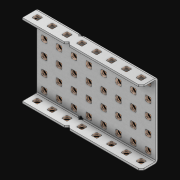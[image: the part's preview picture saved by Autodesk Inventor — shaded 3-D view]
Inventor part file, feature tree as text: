
AUTODESK INVENTOR PART (.ipt)
format: ipt  version: 2021 (Build 250183000, 183)  size: 3,014,144 bytes
history: native  units: in
note: dims shown in document units (in); Inventor stores cm internally (conversion verified against a paired STEP export)
features: extrude x57, other x56, sketch x4, thicken_offset x3, pattern_linear x3, imported_body x1
ambient origin geometry x8: Origin, YZ Plane, XZ Plane, XY Plane, X Axis, Y Axis, Z Axis, Center Point
bodies: Solid1 (feature_tree)
feature tree (124):
  thicken_offset  "Thicken1"
  thicken_offset  "Thicken2"
  thicken_offset  "Thicken3"
  pattern_linear  "Rectangular Pattern1"  Spacing1=0.001in  [1 undecoded]
  pattern_linear  "Rectangular Pattern2"  Spacing1=0.001in  [1 undecoded]
  pattern_linear  "Rectangular Pattern3"  Spacing1=0.182in  [1 undecoded]
  extrude  "Extrusion1"  Depth=0.063in TaperAngle=0.0deg
  sketch  "Sketch1"  dims[d0=0.001in]
  other  "Srf1"
  sketch  "Sketch2"  dims[d1=0.001in]
  other  "Srf2"
  sketch  "Sketch3"  dims[d2=0.001in]
  other  "Srf3"
  other  "Srf4"
  other  "Srf5"
  other  "Srf6"
  other  "Srf7"
  other  "Srf8"
  other  "Srf9"
  other  "Srf10"
  other  "Srf38"
  other  "Srf39"
  other  "Srf40"
  other  "Srf41"
  other  "Srf42"
  other  "Srf43"
  other  "Srf44"
  other  "Srf72"
  other  "Srf73"
  other  "Srf74"
  other  "Srf75"
  other  "Srf76"
  other  "Srf77"
  other  "Srf78"
  other  "Srf106"
  other  "Srf107"
  other  "Srf108"
  other  "Srf109"
  other  "Srf110"
  other  "Srf111"
  other  "Srf112"
  other  "Srf113"
  other  "Srf141"
  other  "Srf142"
  other  "Srf143"
  other  "Srf144"
  other  "Srf145"
  other  "Srf146"
  other  "Srf147"
  other  "Srf148"
  other  "Srf176"
  other  "Srf177"
  other  "Srf178"
  other  "Srf179"
  other  "Srf180"
  other  "Srf181"
  other  "Srf182"
  other  "Srf183"
  other  "Srf211"
  other  "Srf212"
  other  "Srf213"
  other  "Srf214"
  other  "Srf215"
  other  "Srf216"
  other  "Srf217"
  other  "Srf218"
  sketch  "Sketch4"  dims[d3=0.001in d4=0.001in d5=0.001in d6=0.182in d7=0.063in d8=0.0in d9=0.182in d10=0.063in d11=0.0in d12=0.182in d13=0.063in d14=0.0in d17=0.5in d18=3.1496in d20=0.5in d21=3.1496in d23=0.5in d24=1.9685in d26=0.5in d27=13.5in d28=0.0in]
  imported_body  "Imported1"
  extrude  "ExtrusionSrf1"  Depth=0.063in
  extrude  "ExtrusionSrf2"  Depth=0.063in TaperAngle=0.0deg
  extrude  "ExtrusionSrf3"  Depth=0.063in
  extrude  "ExtrusionSrf4"  Depth=0.063in TaperAngle=0.0deg
  extrude  "ExtrusionSrf5"  Depth=0.063in
  extrude  "ExtrusionSrf6"  Depth=0.063in
  extrude  "ExtrusionSrf7"  Depth=0.063in
  extrude  "ExtrusionSrf8"  Depth=0.063in
  extrude  "ExtrusionSrf9"  Depth=0.063in
  extrude  "ExtrusionSrf10"  Depth=0.063in
  extrude  "ExtrusionSrf38"  Depth=0.063in
  extrude  "ExtrusionSrf39"  TaperAngle=0.0deg  [1 undecoded]
  extrude  "ExtrusionSrf40"  [1 undecoded]
  extrude  "ExtrusionSrf41"  [1 undecoded]
  extrude  "ExtrusionSrf42"  [1 undecoded]
  extrude  "ExtrusionSrf43"  [1 undecoded]
  extrude  "ExtrusionSrf44"  [1 undecoded]
  extrude  "ExtrusionSrf72"  [1 undecoded]
  extrude  "ExtrusionSrf73"  [1 undecoded]
  extrude  "ExtrusionSrf74"  [1 undecoded]
  extrude  "ExtrusionSrf75"  [1 undecoded]
  extrude  "ExtrusionSrf76"  [1 undecoded]
  extrude  "ExtrusionSrf77"  [1 undecoded]
  extrude  "ExtrusionSrf78"  [1 undecoded]
  extrude  "ExtrusionSrf106"  [1 undecoded]
  extrude  "ExtrusionSrf107"  [1 undecoded]
  extrude  "ExtrusionSrf108"  [1 undecoded]
  extrude  "ExtrusionSrf109"  [1 undecoded]
  extrude  "ExtrusionSrf110"  [1 undecoded]
  extrude  "ExtrusionSrf111"  [1 undecoded]
  extrude  "ExtrusionSrf112"  [1 undecoded]
  extrude  "ExtrusionSrf113"  [1 undecoded]
  extrude  "ExtrusionSrf141"  [1 undecoded]
  extrude  "ExtrusionSrf142"  [1 undecoded]
  extrude  "ExtrusionSrf143"  [1 undecoded]
  extrude  "ExtrusionSrf144"  [1 undecoded]
  extrude  "ExtrusionSrf145"  [1 undecoded]
  extrude  "ExtrusionSrf146"  [1 undecoded]
  extrude  "ExtrusionSrf147"  [1 undecoded]
  extrude  "ExtrusionSrf148"  [1 undecoded]
  extrude  "ExtrusionSrf176"  [1 undecoded]
  extrude  "ExtrusionSrf177"  [1 undecoded]
  extrude  "ExtrusionSrf178"  [1 undecoded]
  extrude  "ExtrusionSrf179"  [1 undecoded]
  extrude  "ExtrusionSrf180"  [1 undecoded]
  extrude  "ExtrusionSrf181"  [1 undecoded]
  extrude  "ExtrusionSrf182"  [1 undecoded]
  extrude  "ExtrusionSrf183"  [1 undecoded]
  extrude  "ExtrusionSrf211"  [1 undecoded]
  extrude  "ExtrusionSrf212"  [1 undecoded]
  extrude  "ExtrusionSrf213"  [1 undecoded]
  extrude  "ExtrusionSrf214"  [1 undecoded]
  extrude  "ExtrusionSrf215"  [1 undecoded]
  extrude  "ExtrusionSrf216"  [1 undecoded]
  extrude  "ExtrusionSrf217"  [1 undecoded]
  extrude  "ExtrusionSrf218"  [1 undecoded]
note: 48 required parameter values undecoded (feature->parameter linkage not recoverable at this tier; creation-order binding heuristic only, values carry confidence <= 0.55)
